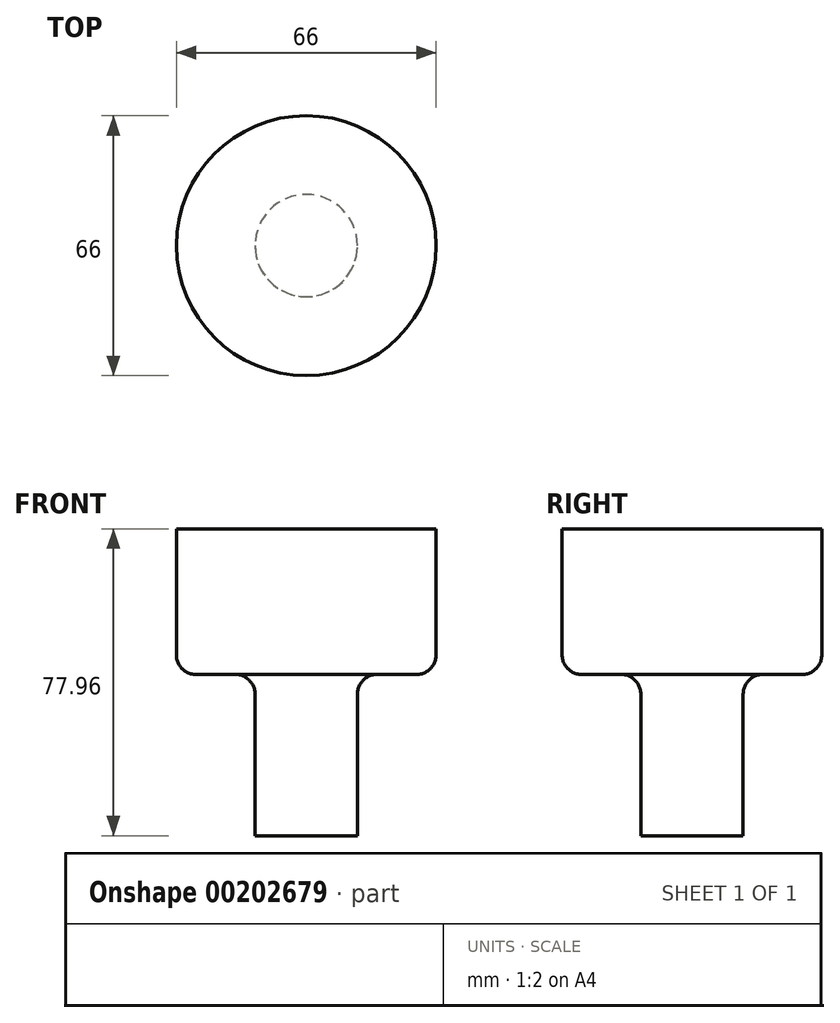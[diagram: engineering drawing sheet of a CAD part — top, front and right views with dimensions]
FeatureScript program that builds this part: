
annotation { "Feature Type Name" : "Feature", "Feature Type Description" : "" }
export const myFeature = defineFeature(function(context is Context, id is Id, definition is map)
    precondition{}
    {
        {
            var Q0;
            Q0=qCreatedBy(makeId("Front.planeOp"),FACE);
            var sketch = newSketch(context, id + "F0", { "sketchPlane" : qUnion([Q0])});
            skLineSegment(sketch, "E0", {"start": v(0, -72.8) * mm, "end": v(0, 57.2) * mm, "construction": true});
            skLineSegment(sketch, "E1", {"start": v(0, 57.2) * mm, "end": v(-35, 57.2) * mm, "construction": true});
            skLineSegment(sketch, "E2", {"start": v(-35, 57.2) * mm, "end": v(-35, 7.2) * mm});
            skLineSegment(sketch, "E3", {"start": v(-35, 7.2) * mm, "end": v(-15, 7.2) * mm});
            skLineSegment(sketch, "E4", {"start": v(-15, 7.2) * mm, "end": v(-15, -72.8) * mm});
            skLineSegment(sketch, "E5", {"start": v(-15, -72.8) * mm, "end": v(0, -72.8) * mm, "construction": true});
            skLineSegment(sketch, "E6.0", {"start": v(-13, 9.2) * mm, "end": v(-13, -72.8) * mm});
            skLineSegment(sketch, "E6.1", {"start": v(-33, 9.2) * mm, "end": v(-13, 9.2) * mm});
            skLineSegment(sketch, "E6.2", {"start": v(-33, 57.2) * mm, "end": v(-33, 9.2) * mm});
            skLineSegment(sketch, "E7", {"start": v(-35, 57.2) * mm, "end": v(-33, 57.2) * mm});
            skLineSegment(sketch, "E8", {"start": v(-15, -72.8) * mm, "end": v(-13, -72.8) * mm});
            skSolve(sketch);
        }
        {
            var Q0;
            Q0=qCreatedBy(makeId("Front.planeOp"),FACE);
            var sketch = newSketch(context, id + "F1", { "sketchPlane" : qUnion([Q0])});
            skPoint(sketch, "E9.start.orphan", {"position": v(-16.79, 11.78) * mm});
            skPoint(sketch, "E10.start.orphan", {"position": v(0, 11.78) * mm});
            skLineSegment(sketch, "E11.0", {"start": v(-13, 9.2) * mm, "end": v(-13, -31.8) * mm});
            skLineSegment(sketch, "E12", {"start": v(-13, -31.8) * mm, "end": v(0, -31.8) * mm});
            skLineSegment(sketch, "E13", {"start": v(0, 9.2) * mm, "end": v(0, -31.8) * mm});
            skPoint(sketch, "E14.orphan", {"position": v(-13, -72.8) * mm});
            skLineSegment(sketch, "E15.0", {"start": v(-33, 9.2) * mm, "end": v(-13, 9.2) * mm});
            skLineSegment(sketch, "E16.0", {"start": v(-33, 46.16) * mm, "end": v(-33, 9.2) * mm});
            skLineSegment(sketch, "E17", {"start": v(0, 9.2) * mm, "end": v(0, 46.16) * mm});
            skLineSegment(sketch, "E18", {"start": v(-33, 46.16) * mm, "end": v(0, 46.16) * mm});
            skPoint(sketch, "E19.end.orphan", {"position": v(-33, 57.2) * mm});
            skSolve(sketch);
        }
        {
            var Q0;
            Q0=makeQuery(id+"F1.imprint","IMPRINT",FACE,{"disambiguationData":[TD([[makeQuery(id+"F1.imprint","IMPRINT",EDGE,{"derivedFrom":sQuery(id+"F1.wireOp",EDGE,"E11.0")}),1.0]])]});
            var Q1;
            Q1=sQuery(id+"F1.wireOp",EDGE,"E17");
            revolve(context, id + "F2", {"entities" : qUnion([Q0]), "axis" : qUnion([Q1]), "revolveType" : RevolveType.FULL});
        }
        {
            var Q0;
            Q0=makeQuery(id+"F2.opRevolve","SWEPT_EDGE",EDGE,{"disambiguationData":[OSD([sQuery(id+"F1.wireOp",EDGE,"E11.0"),sQuery(id+"F1.wireOp",EDGE,"E15.0")])]});
            var Q1;
            Q1=makeQuery(id+"F2.opRevolve","SWEPT_EDGE",EDGE,{"disambiguationData":[OSD([sQuery(id+"F1.wireOp",EDGE,"E15.0"),sQuery(id+"F1.wireOp",EDGE,"E16.0")])]});
            fillet(context, id + "F3", {"entities" : qUnion([Q0, Q1]), "radius" : 5 * mm, "tangentPropagation" : true, "allowEdgeOverflow" : false});
        }
    });
